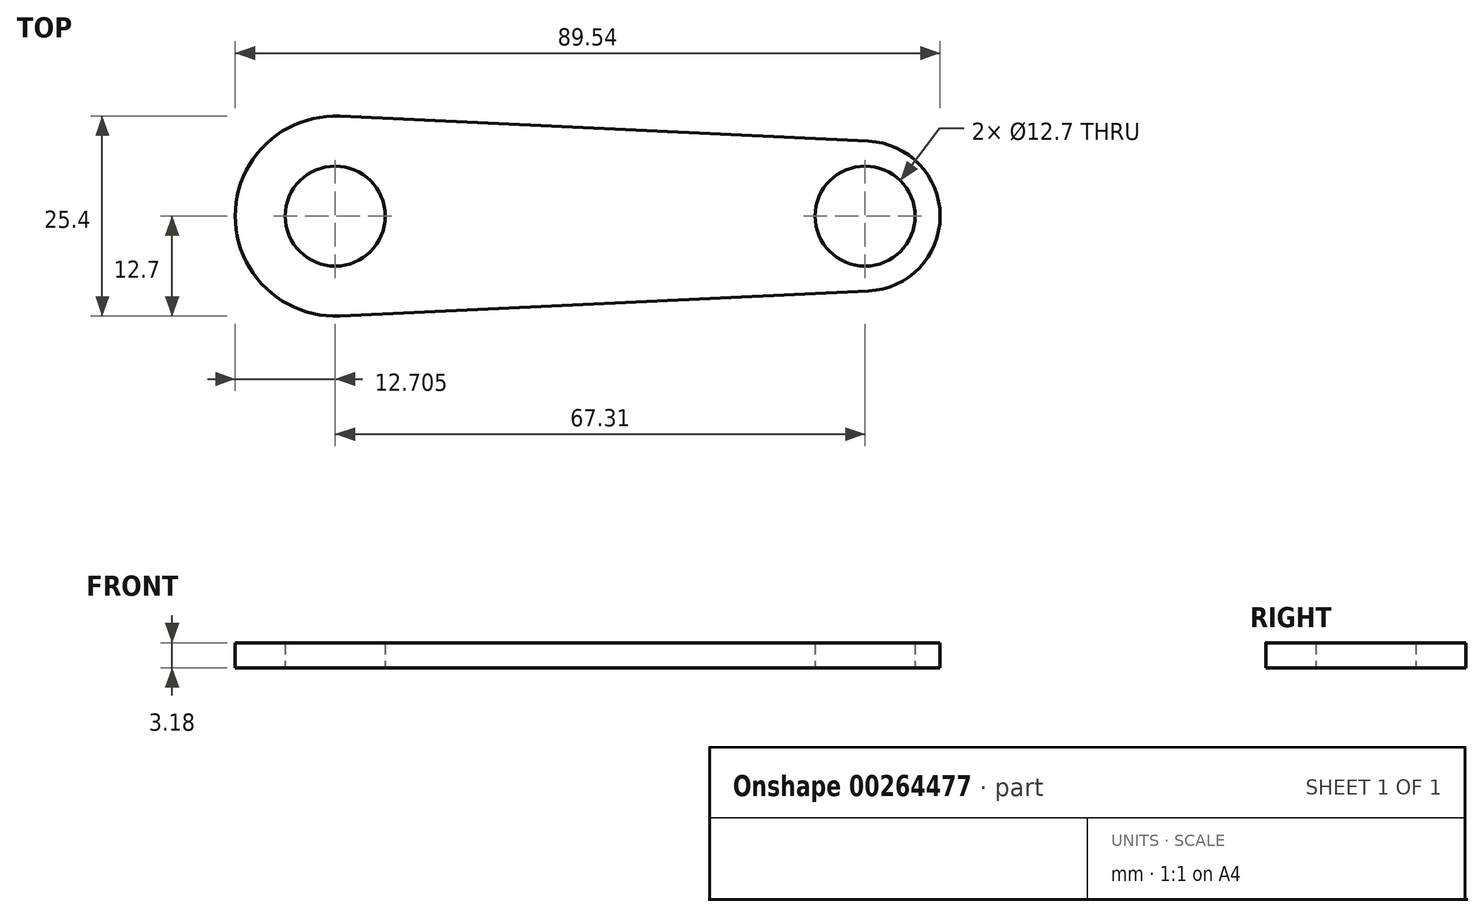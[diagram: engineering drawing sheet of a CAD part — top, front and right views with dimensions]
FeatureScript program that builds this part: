
annotation { "Feature Type Name" : "Feature", "Feature Type Description" : "" }
export const myFeature = defineFeature(function(context is Context, id is Id, definition is map)
    precondition{}
    {
        {
            var Q0;
            Q0=qCreatedBy(makeId("Top.planeOp"),FACE);
            var sketch = newSketch(context, id + "F0", { "sketchPlane" : qUnion([Q0])});
            skCircle(sketch, "E0", {"center": v(-47.63, 0) * mm, "radius": 12.7 * mm});
            skCircle(sketch, "E1", {"center": v(19.69, 0) * mm, "radius": 9.53 * mm});
            skLineSegment(sketch, "E2", {"start": v(-47.63, 0) * mm, "end": v(19.69, 0) * mm});
            skLineSegment(sketch, "E3", {"start": v(-47.03, -12.69) * mm, "end": v(20.13, -9.51) * mm});
            skLineSegment(sketch, "E4", {"start": v(-47.03, 12.69) * mm, "end": v(20.13, 9.51) * mm});
            skCircle(sketch, "E5", {"center": v(-47.63, 0) * mm, "radius": 6.35 * mm});
            skCircle(sketch, "E6", {"center": v(19.69, 0) * mm, "radius": 6.35 * mm});
            skSolve(sketch);
        }
        {
            var Q0;
            {var subQ0=sQuery(id+"F0.wireOp",EDGE,"E4");Q0=makeQuery(id+"F0.imprint","IMPRINT",FACE,{"disambiguationData":[TD([[makeQuery(id+"F0.imprint","IMPRINT",EDGE,{"derivedFrom":subQ0}),-1.0]])]});}
            var Q1;
            {var subQ0=sQuery(id+"F0.wireOp",EDGE,"E3");Q1=makeQuery(id+"F0.imprint","IMPRINT",FACE,{"disambiguationData":[TD([[makeQuery(id+"F0.imprint","IMPRINT",EDGE,{"derivedFrom":subQ0}),1.0]])]});}
            var Q2;
            Q2=makeQuery(id+"F0.imprint","IMPRINT",FACE,{"disambiguationData":[TD([[makeQuery(id+"F0.imprint","IMPRINT",EDGE,{"derivedFrom":sQuery(id+"F0.wireOp",EDGE,"E5")}),-1.0]])]});
            var Q3;
            Q3=makeQuery(id+"F0.imprint","IMPRINT",FACE,{"disambiguationData":[TD([[makeQuery(id+"F0.imprint","IMPRINT",EDGE,{"derivedFrom":sQuery(id+"F0.wireOp",EDGE,"E6")}),-1.0]])]});
            extrude(context, id + "F1", {"entities" : qUnion([Q0, Q1, Q2, Q3]), "depth" : 3.17 * mm});
        }
    });
